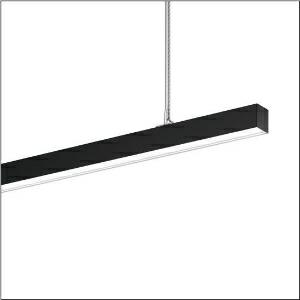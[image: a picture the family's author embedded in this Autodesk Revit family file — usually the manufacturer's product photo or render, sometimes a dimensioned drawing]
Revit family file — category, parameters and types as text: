
# Revit family: silica_r__21_51mx33tctdb_eeca
name_source: partatom
category: Lighting Fixtures
units: mm (PartAtom-declared; Revit-internal decimal feet)

## family parameters
Cut with Voids When Loaded = No
Host = Face
Light Source = No
Part Type = Normal
Room Calculation Point = No
Round Connector Dimension = Use Diameter
Shared = No

## types (1)
- --- (1 x LED, 14340 lm, 134.7 W, 6500K)
    Apparent Load = 135 VA
    CIE Flux Codes = 78 96 99 56 100
    Color Rendering = 80
    Color Temperature = 6500K
    Default Elevation = 1800 mm
    Description = Silica® 21, office luminaire, primary optical cover: prismatic diffuser, of PMMA, CAT 2 (L<= 3000cd/m²), light emission: direct/indirect distribution, primary light characteristic: symmetric, installation type: suspended mounting, LED, rated luminous flux: 14.340lm, luminous efficacy: 101lm/W, light colour: 8tw, colour temperature: 2700..6500K, control gear: ECG DALI, with terminal, 3+2-pole, max. 2.5mm², mains connection: 220..240V, AC, 50/60Hz, rated input power: 141.4W, luminaire housing, of aluminium, jet black (RAL 9005), length: 3.004mm, width: 53mm, height: 53mm, protection rating (complete): IP20, insulation class (complete): insulation class I (protective earthing), certification: CE, permissible operating ambient temperature: 0..+35°C, standard: EN 50419, packaging unit: 1 piece
    Height = 53 mm
    Lamp = 1 x LED
    Lamp Light Flux = 14340 lm
    Lamp Power = 134.7 W
    Lamp count = 1
    Length = 3004 mm
    Luminous efficacy = 106 lm/W
    Manufacturer = Siteco
    ModVariant = No
    Model = 51MX33TCTDB
    Mounting Place = Ceiling
    Mounting Type = Pendant
    Number of Poles = 1
    OnlyDefault = Yes
    Power Factor = 1
    Product Name = Silica® 21
    Product group = office luminaire | ceiling pendant
    ProductGroupID = 905
    Protection Class = Protection class I
    Protection Degree = IP 20
    RLX_Detail_Level = 1
    RlxData = <blob elided: 22845 chars, md5=9aa8e010>
    Socket = socket
    Standby Power = 0 W
    System Light Flux = 14340 lm
    System Power = 135 W
    Type Comments = individual setting
    Type Image = l_1251735.jpg
    URL = http://relux.com
    VarID = @adj_045843
    Voltage = 0 V
    Weight = 0.00 kg
    Width = 53 mm

## geometry (parser evidence)
native form markers: Blend x4, Sweep x11
no freeform markers — native parametric forms only
